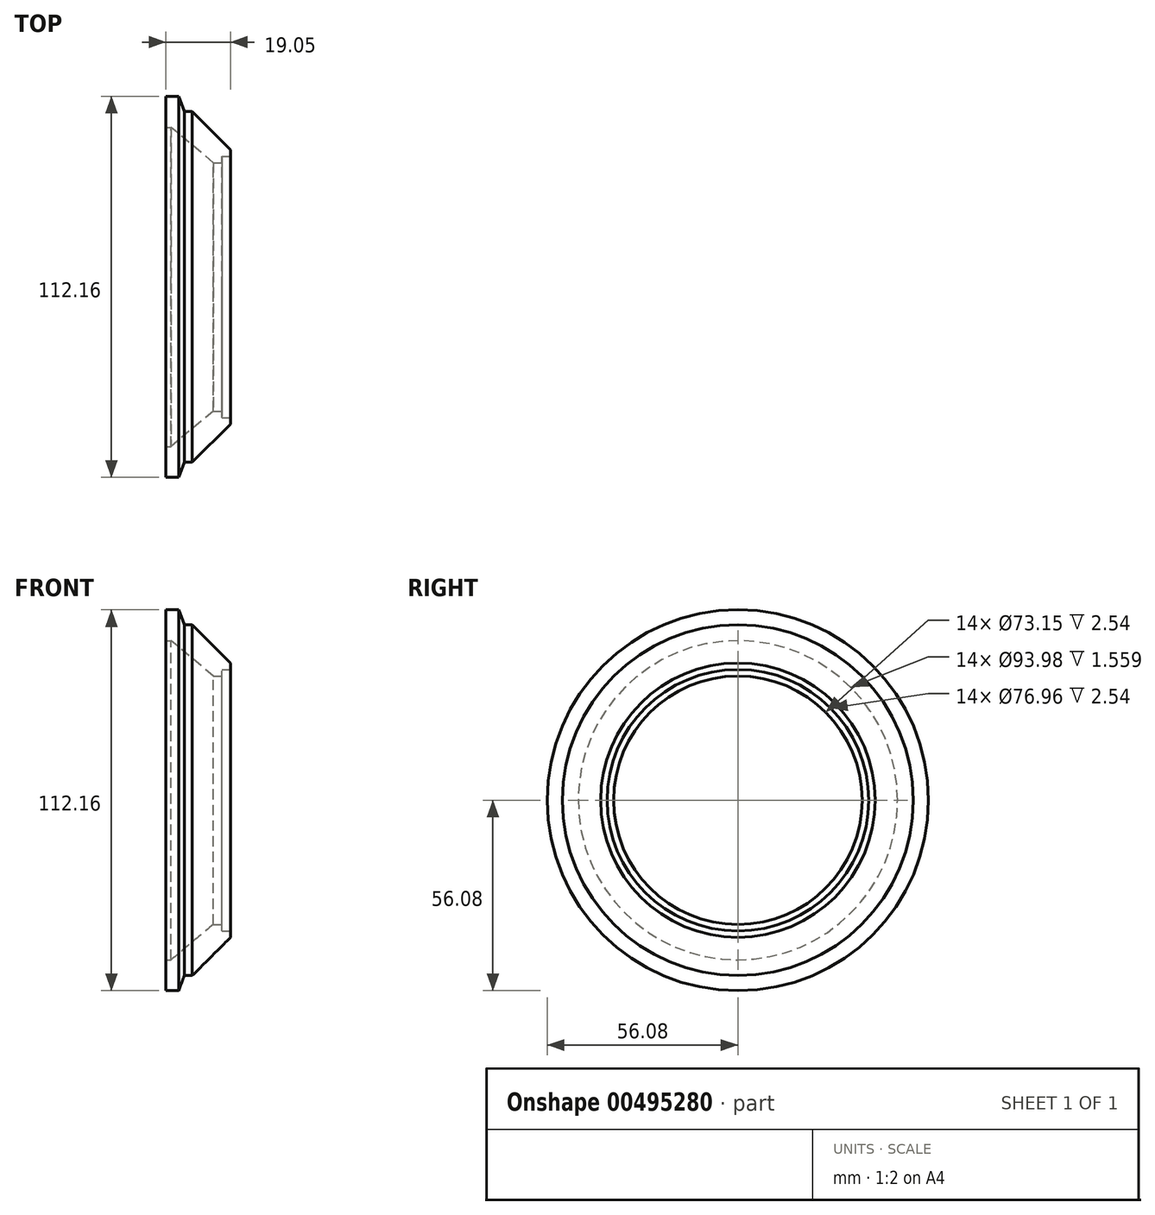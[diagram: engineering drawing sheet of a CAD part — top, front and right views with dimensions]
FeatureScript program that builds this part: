
annotation { "Feature Type Name" : "Feature", "Feature Type Description" : "" }
export const myFeature = defineFeature(function(context is Context, id is Id, definition is map)
    precondition{}
    {
        {
            var Q0;
            Q0=qCreatedBy(makeId("Front.planeOp"),FACE);
            var sketch = newSketch(context, id + "F0", { "sketchPlane" : qUnion([Q0])});
            skLineSegment(sketch, "E0", {"start": v(0, 0) * mm, "end": v(67.1, 0) * mm, "construction": true});
            skLineSegment(sketch, "E1", {"start": v(67.1, 0) * mm, "end": v(0, 0) * mm, "construction": true});
            skLineSegment(sketch, "E2", {"start": v(0, 56.08) * mm, "end": v(0, 0) * mm, "construction": true});
            skLineSegment(sketch, "E3", {"start": v(0, 56.08) * mm, "end": v(3.8, 56.08) * mm});
            skLineSegment(sketch, "E4", {"start": v(3.8, 56.08) * mm, "end": v(5.43, 51.64) * mm});
            skLineSegment(sketch, "E5", {"start": v(5.43, 51.64) * mm, "end": v(7.8, 51.64) * mm});
            skLineSegment(sketch, "E6", {"start": v(0, 56.08) * mm, "end": v(0, 47) * mm});
            skLineSegment(sketch, "E7", {"start": v(0, 47) * mm, "end": v(1.56, 47) * mm});
            skPoint(sketch, "E8.end.orphan", {"position": v(7.8, 44.5) * mm});
            skLineSegment(sketch, "E9", {"start": v(13.97, 36.58) * mm, "end": v(1.56, 46.99) * mm});
            skLineSegment(sketch, "E10", {"start": v(7.8, 51.64) * mm, "end": v(19.05, 40.39) * mm});
            skLineSegment(sketch, "E11", {"start": v(19.05, 40.39) * mm, "end": v(19.05, 36.58) * mm});
            skLineSegment(sketch, "E12", {"start": v(19.05, 36.58) * mm, "end": v(13.97, 36.58) * mm});
            skSolve(sketch);
        }
        {
            var Q0;
            Q0=makeQuery(id+"F0.imprint","IMPRINT",FACE,{"disambiguationData":[TD([[makeQuery(id+"F0.imprint","IMPRINT",EDGE,{"derivedFrom":sQuery(id+"F0.wireOp",EDGE,"E3")}),-1.0]])]});
            var Q1;
            Q1=sQuery(id+"F0.wireOp",EDGE,"E1");
            revolve(context, id + "F1", {"entities" : qUnion([Q0]), "axis" : qUnion([Q1]), "revolveType" : RevolveType.FULL});
        }
        {
            var Q0;
            Q0=makeQuery(id+"F1.opRevolve","SWEPT_FACE",FACE,{"disambiguationData":[OSD([sQuery(id+"F0.wireOp",EDGE,"E11")])]});
            var sketch = newSketch(context, id + "F2", { "sketchPlane" : qUnion([Q0])});
            skCircle(sketch, "E13", {"center": v(0, 0) * mm, "radius": 38.48 * mm});
            skSolve(sketch);
        }
        {
            var Q0;
            Q0 = qSketchRegion(id + "F2", true);
            extrude(context, id + "F3", {"entities" : qUnion([Q0]), "operationType" : NewBodyOperationType.REMOVE, "oppositeDirection" : true, "depth" : 2.54 * mm});
        }
    });
